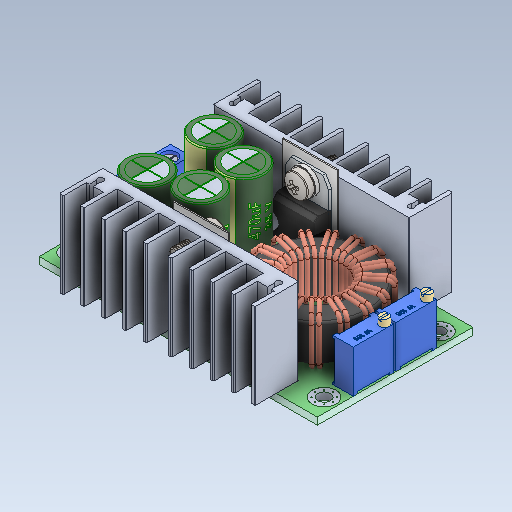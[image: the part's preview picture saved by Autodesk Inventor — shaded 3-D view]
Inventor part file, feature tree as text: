
AUTODESK INVENTOR PART (.ipt)
format: ipt  version: 2020 (Build 240168000, 168)  size: 7,680,512 bytes
history: native  units: in
note: dims shown in document units (in); Inventor stores cm internally (conversion verified against a paired STEP export)
features: other x128, helix x20, surface_op x10
ambient origin geometry x8: Origin, YZ Plane, XZ Plane, XY Plane, X Axis, Y Axis, Z Axis, Center Point
bodies: Solid1 (feature_tree), Solid2 (feature_tree), Solid3 (feature_tree), Solid4 (feature_tree), Solid5 (feature_tree), Solid6 (feature_tree), Solid7 (feature_tree), Solid8 (feature_tree), Solid9 (feature_tree), Solid10 (feature_tree), Solid11 (feature_tree), Solid12 (feature_tree), Solid13 (feature_tree), Solid14 (feature_tree), Solid15 (feature_tree), Solid16 (feature_tree), Solid17 (feature_tree), Solid18 (feature_tree), Solid19 (feature_tree), Solid20 (feature_tree), Solid21 (feature_tree), Solid22 (feature_tree), Solid23 (feature_tree), Solid24 (feature_tree), Solid25 (feature_tree), Solid26 (feature_tree), Solid27 (feature_tree), Solid28 (feature_tree), Solid29 (feature_tree), Solid30 (feature_tree), Solid31 (feature_tree), Solid32 (feature_tree), Solid33 (feature_tree), Solid34 (feature_tree), Solid35 (feature_tree), Solid36 (feature_tree), Solid37 (feature_tree), Solid38 (feature_tree), Solid39 (feature_tree), Solid40 (feature_tree), Solid41 (feature_tree), Solid42 (feature_tree), Solid43 (feature_tree), Solid44 (feature_tree), Solid45 (feature_tree), Solid46 (feature_tree), Solid47 (feature_tree), Solid48 (feature_tree), Solid49 (feature_tree), Solid50 (feature_tree), Solid51 (feature_tree), Solid52 (feature_tree), Solid53 (feature_tree), Solid54 (feature_tree), Solid55 (feature_tree), Solid56 (feature_tree), Solid57 (feature_tree), Solid58 (feature_tree), Solid59 (feature_tree), Solid60 (feature_tree), Solid61 (feature_tree), Solid62 (feature_tree), Solid63 (feature_tree), Solid64 (feature_tree), Solid65 (feature_tree), Solid66 (feature_tree), Solid67 (feature_tree), Solid68 (feature_tree), Solid69 (feature_tree), Solid70 (feature_tree), Solid71 (feature_tree), Solid72 (feature_tree), Solid73 (feature_tree), Solid74 (feature_tree), Solid75 (feature_tree), Solid76 (feature_tree), Solid77 (feature_tree), Solid78 (feature_tree), Solid79 (feature_tree), Solid80 (feature_tree), Solid81 (feature_tree), Solid82 (feature_tree), Solid83 (feature_tree), Solid84 (feature_tree), Solid85 (feature_tree), Solid86 (feature_tree), Solid87 (feature_tree), Solid88 (feature_tree), Solid89 (feature_tree), Solid90 (feature_tree), Solid91 (feature_tree), Solid92 (feature_tree), Solid93 (feature_tree), Solid94 (feature_tree), Solid95 (feature_tree), Solid96 (feature_tree), Solid97 (feature_tree), Solid98 (feature_tree), Solid99 (feature_tree), Solid100 (feature_tree), Solid101 (feature_tree), Solid102 (feature_tree), Solid103 (feature_tree), Solid104 (feature_tree), Solid105 (feature_tree), Solid106 (feature_tree), Solid107 (feature_tree), Solid108 (feature_tree), Solid109 (feature_tree), Solid110 (feature_tree), Solid111 (feature_tree), Solid112 (feature_tree), Solid113 (feature_tree), Solid114 (feature_tree), Solid115 (feature_tree), Solid116 (feature_tree), Solid117 (feature_tree), Solid118 (feature_tree), Solid119 (feature_tree), Solid120 (feature_tree), Solid121 (feature_tree), Solid122 (feature_tree), Solid123 (feature_tree), Solid124 (feature_tree), Solid125 (feature_tree), Solid126 (feature_tree), Solid127 (feature_tree), Solid128 (feature_tree), Solid129 (feature_tree), Solid130 (feature_tree), Solid131 (feature_tree), Solid132 (feature_tree), Solid133 (feature_tree), Solid134 (feature_tree), Solid135 (feature_tree), Solid136 (feature_tree), Solid137 (feature_tree), Solid138 (feature_tree), Solid139 (feature_tree), Solid140 (feature_tree), Solid141 (feature_tree), Solid142 (feature_tree), Solid143 (feature_tree), Solid144 (feature_tree), Solid145 (feature_tree), Solid146 (feature_tree), Solid147 (feature_tree), Solid148 (feature_tree), Solid149 (feature_tree), Solid150 (feature_tree), Solid151 (feature_tree), Solid152 (feature_tree), Solid153 (feature_tree), Solid154 (feature_tree), Solid155 (feature_tree), Solid156 (feature_tree), Solid157 (feature_tree), Solid158 (feature_tree)
feature tree (158):
  other  "8A Buck Converter PCB_1:1"
  other  "Heat Exchanger_2:1"
  other  "Heat Exchanger_2:2"
  other  "Heat Exchanger_2:3"
  other  "Heat Exchanger_2:4"
  other  "Heat Exchanger_3:1"
  other  "Heat Exchanger_3:2"
  other  "Heat Exchanger_3:3"
  other  "Heat Exchanger_3:4"
  other  "LargeGreen1000uF 35V Electrolytic Capacitor_4:1"
  other  "LargeGreen1000uF 35V Electrolytic Capacitor_5:1"
  other  "LargeGreen470uF 35V Electrolytic Capacitor_6:1"
  other  "LargeGreen470uF 35V Electrolytic Capacitor_7:1"
  other  "Screw Terminal x2_8:1"
  other  "Screw Terminal x2_8:2"
  other  "Screw Terminal x2_8:3"
  other  "Screw Terminal x2_8:4"
  other  "Screw Terminal x2_8:5"
  other  "Screw Terminal x2_9:1"
  other  "Screw Terminal x2_9:2"
  other  "Screw Terminal x2_9:3"
  other  "Screw Terminal x2_9:4"
  other  "Screw Terminal x2_9:5"
  surface_op  "TrimmerW103_10:1"
  surface_op  "TrimmerW103_10:2"
  surface_op  "TrimmerW103_10:3"
  surface_op  "TrimmerW103_10:4"
  surface_op  "TrimmerW103_10:5"
  surface_op  "TrimmerW103_11:1"
  surface_op  "TrimmerW103_11:2"
  surface_op  "TrimmerW103_11:3"
  surface_op  "TrimmerW103_11:4"
  surface_op  "TrimmerW103_11:5"
  other  "whiteLEDShortLeed_12:1"
  other  "whiteLEDShortLeed_12:2"
  other  "whiteLEDShortLeed_12:3"
  other  "Schottky Diode 20A 45V STPS2045CT_13:1"
  other  "Schottky Diode 20A 45V STPS2045CT_13:2"
  other  "Schottky Diode 20A 45V STPS2045CT_13:3"
  other  "Schottky Diode 20A 45V STPS2045CT_13:4"
  other  "Schottky Diode 20A 45V STPS2045CT_13:5"
  other  "XL4016E1 8A Voltage Regulator_14:1"
  other  "XL4016E1 8A Voltage Regulator_14:2"
  other  "XL4016E1 8A Voltage Regulator_14:3"
  other  "XL4016E1 8A Voltage Regulator_14:4"
  other  "XL4016E1 8A Voltage Regulator_14:5"
  other  "XL4016E1 8A Voltage Regulator_14:6"
  other  "XL4016E1 8A Voltage Regulator_14:7"
  helix  "Coil for Convertor_15:1"  [1 undecoded]
  helix  "Coil for Convertor_15:2"  [1 undecoded]
  helix  "Coil for Convertor_15:3"  [1 undecoded]
  helix  "Coil for Convertor_15:4"  [1 undecoded]
  helix  "Coil for Convertor_15:5"  [1 undecoded]
  helix  "Coil for Convertor_15:6"  [1 undecoded]
  helix  "Coil for Convertor_15:7"  [1 undecoded]
  helix  "Coil for Convertor_15:8"  [1 undecoded]
  helix  "Coil for Convertor_15:9"  [1 undecoded]
  helix  "Coil for Convertor_15:10"  [1 undecoded]
  helix  "Coil for Convertor_15:11"  [1 undecoded]
  helix  "Coil for Convertor_15:12"  [1 undecoded]
  helix  "Coil for Convertor_15:13"  [1 undecoded]
  helix  "Coil for Convertor_15:14"  [1 undecoded]
  helix  "Coil for Convertor_15:15"  [1 undecoded]
  helix  "Coil for Convertor_15:16"  [1 undecoded]
  helix  "Coil for Convertor_15:17"  [1 undecoded]
  helix  "Coil for Convertor_15:18"  [1 undecoded]
  helix  "Coil for Convertor_15:19"  [1 undecoded]
  helix  "Coil for Convertor_15:20"  [1 undecoded]
  other  "Small Plastic Washer_16:1"
  other  "Small Plastic Washer_17:1"
  other  "pan head cross recess screw_iso_ISO 7045 - M3 x 8 - Z - 8S_18:1"
  other  "pan head cross recess screw_iso_ISO 7045 - M3 x 8 - Z - 8S_19:1"
  other  "1.7mmSmdCeramicCapacitorbrown_20:1"
  other  "1.7mmSmdCeramicCapacitorbrown_20:2"
  other  "1.7mmSmdCeramicCapacitorbrown_20:3"
  other  "smdChip8pin_21:1"
  other  "smdChip8pin_21:2"
  other  "smdChip8pin_21:3"
  other  "smdChip8pin_21:4"
  other  "smdChip8pin_21:5"
  other  "smdChip8pin_21:6"
  other  "smdChip8pin_21:7"
  other  "smdChip8pin_21:8"
  other  "smdChip8pin_21:9"
  other  "tinyVoltageRegulator_22:1"
  other  "tinyVoltageRegulator_22:2"
  other  "tinyVoltageRegulator_22:3"
  other  "tinyVoltageRegulator_22:4"
  other  "tinyVoltageRegulator_23:1"
  other  "tinyVoltageRegulator_23:2"
  other  "tinyVoltageRegulator_23:3"
  other  "tinyVoltageRegulator_23:4"
  other  "TinyVoltageRegulatorAMS1112_24:1"
  other  "tinySMDResistor222_25:1"
  other  "tinySMDResistor_26:1"
  other  "1.7mmSmdCeramicCapacitorbrown_27:1"
  other  "1.7mmSmdCeramicCapacitorbrown_27:2"
  other  "1.7mmSmdCeramicCapacitorbrown_27:3"
  other  "1.7mmSmdCeramicCapacitorbrown_28:1"
  other  "1.7mmSmdCeramicCapacitorbrown_28:2"
  other  "1.7mmSmdCeramicCapacitorbrown_28:3"
  other  "1.7mmSmdCeramicCapacitorbrown_29:1"
  other  "1.7mmSmdCeramicCapacitorbrown_29:2"
  other  "1.7mmSmdCeramicCapacitorbrown_29:3"
  other  "tinySMDResistor_30:1"
  other  "tinySMDResistor_31:1"
  other  "tinySMDResistor_32:1"
  other  "1.7mmSmdCeramicCapacitorbrown_33:1"
  other  "1.7mmSmdCeramicCapacitorbrown_33:2"
  other  "1.7mmSmdCeramicCapacitorbrown_33:3"
  other  "1.7mmSmdCeramicCapacitorbrown_34:1"
  other  "1.7mmSmdCeramicCapacitorbrown_34:2"
  other  "1.7mmSmdCeramicCapacitorbrown_34:3"
  other  "1.7mmSmdCeramicCapacitorbrown_35:1"
  other  "1.7mmSmdCeramicCapacitorbrown_35:2"
  other  "1.7mmSmdCeramicCapacitorbrown_35:3"
  other  "1.7mmSmdCeramicCapacitorbrown_36:1"
  other  "1.7mmSmdCeramicCapacitorbrown_36:2"
  other  "1.7mmSmdCeramicCapacitorbrown_36:3"
  other  "tinySMDResistor_37:1"
  other  "tinySMDResistor_38:1"
  other  "tinySMDResistor_39:1"
  other  "tinySMDResistor_40:1"
  other  "R010 Resistor SMD_41:1"
  other  "solder_42:1"
  other  "solder_43:1"
  other  "solder_44:1"
  other  "solder_45:1"
  other  "solder1.8_46:1"
  other  "solder1.8_47:1"
  other  "solder1.8_48:1"
  other  "solder1.8_49:1"
  other  "solder_50:1"
  other  "solder_51:1"
  other  "solder_52:1"
  other  "solder_53:1"
  other  "solder_54:1"
  other  "solder_55:1"
  other  "solder1.8_56:1"
  other  "solder1.8_57:1"
  other  "solder_58:1"
  other  "solder_59:1"
  other  "solder_60:1"
  other  "solder_61:1"
  other  "solder_62:1"
  other  "solder_63:1"
  other  "solder_64:1"
  other  "solder_65:1"
  other  "solder_66:1"
  other  "solder_67:1"
  other  "solder_68:1"
  other  "solder_69:1"
  other  "solder_70:1"
  other  "solder_71:1"
  other  "solder_72:1"
  other  "solder_73:1"
  other  "solder_74:1"
  other  "solder_75:1"
note: 20 required parameter values undecoded (feature->parameter linkage not recoverable at this tier; creation-order binding heuristic only, values carry confidence <= 0.55)
